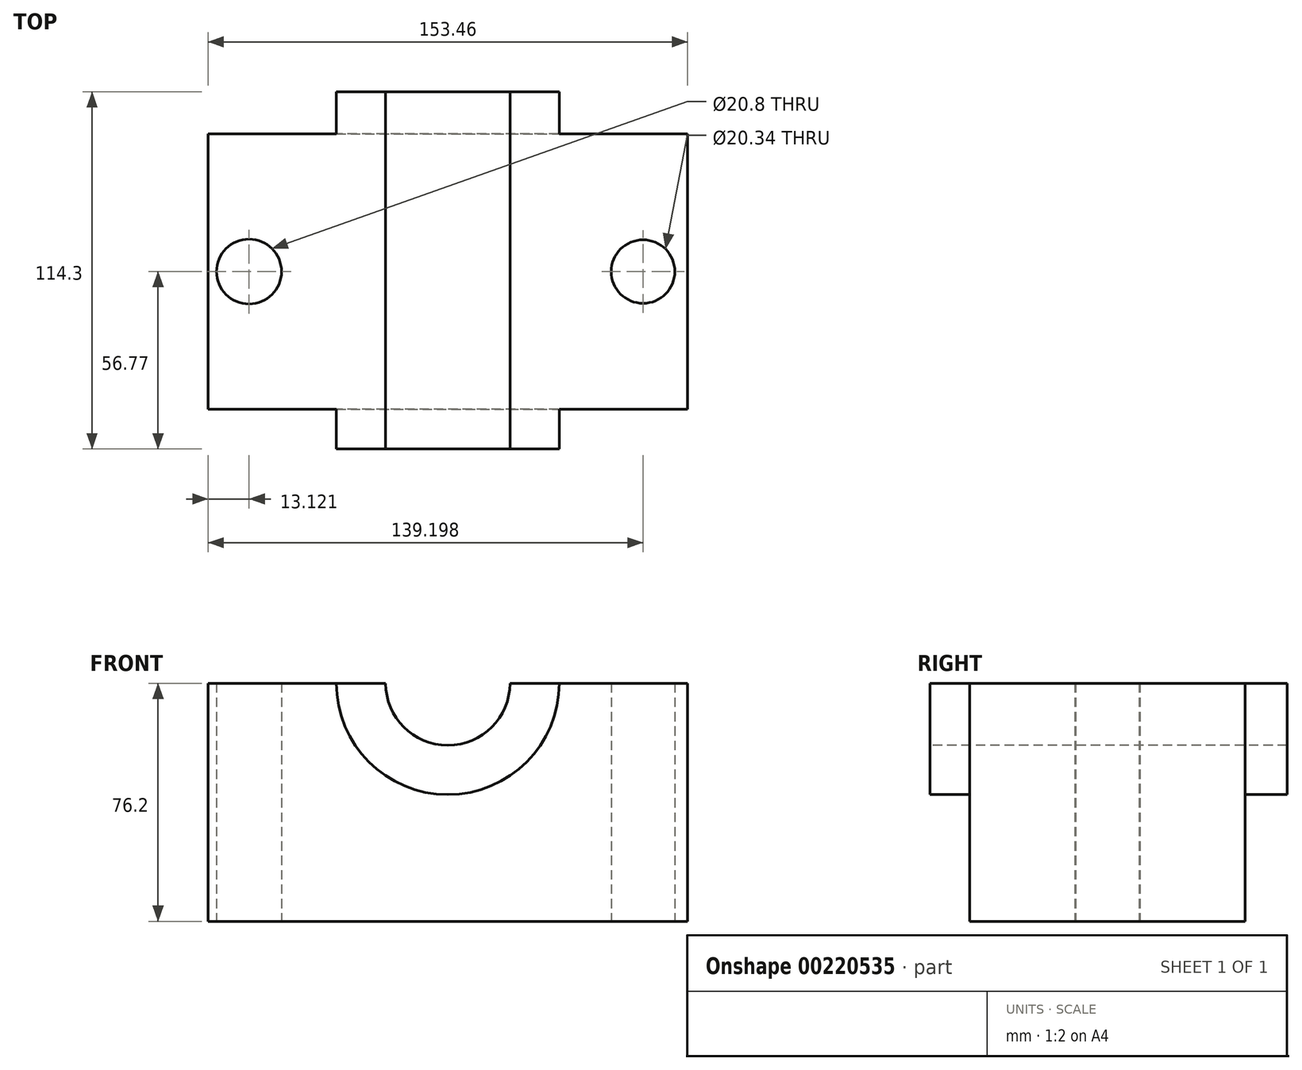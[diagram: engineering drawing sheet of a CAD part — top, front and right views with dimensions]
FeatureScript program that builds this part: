
annotation { "Feature Type Name" : "Feature", "Feature Type Description" : "" }
export const myFeature = defineFeature(function(context is Context, id is Id, definition is map)
    precondition{}
    {
        {
            var Q0;
            Q0=qCreatedBy(makeId("Top.planeOp"),FACE);
            var sketch = newSketch(context, id + "F0", { "sketchPlane" : qUnion([Q0])});
            skLineSegment(sketch, "E0.bottom", {"start": v(76.73, 44.07) * mm, "end": v(-76.73, 44.07) * mm});
            skLineSegment(sketch, "E0.top", {"start": v(76.73, -44.07) * mm, "end": v(-76.73, -44.07) * mm});
            skLineSegment(sketch, "E0.left", {"start": v(76.73, 44.07) * mm, "end": v(76.73, -44.07) * mm});
            skLineSegment(sketch, "E0.right", {"start": v(-76.73, 44.07) * mm, "end": v(-76.73, -44.07) * mm});
            skPoint(sketch, "E0.middle", {"position": v(0, 0) * mm});
            skSolve(sketch);
        }
        {
            var Q0;
            Q0=makeQuery(id+"F0.imprint","IMPRINT",FACE,{"disambiguationData":[TD([[makeQuery(id+"F0.imprint","IMPRINT",EDGE,{"derivedFrom":sQuery(id+"F0.wireOp",EDGE,"E0.bottom")}),1.0]])]});
            var sketch = newSketch(context, id + "F1", { "sketchPlane" : qUnion([Q0])});
            skCircle(sketch, "E1", {"center": v(-63.6, 0) * mm, "radius": 10.4 * mm});
            skCircle(sketch, "E2", {"center": v(62.47, 0) * mm, "radius": 10.17 * mm});
            skSolve(sketch);
        }
        {
            var Q0;
            Q0=makeQuery(id+"F0.imprint","IMPRINT",FACE,{"disambiguationData":[TD([[makeQuery(id+"F0.imprint","IMPRINT",EDGE,{"derivedFrom":sQuery(id+"F0.wireOp",EDGE,"E0.bottom")}),1.0]])]});
            extrude(context, id + "F2", {"entities" : qUnion([Q0]), "depth" : 76.2 * mm});
        }
        {
            var Q0;
            Q0=makeQuery(id+"F1.imprint","IMPRINT",FACE,{"disambiguationData":[TD([[makeQuery(id+"F1.imprint","IMPRINT",EDGE,{"derivedFrom":sQuery(id+"F1.wireOp",EDGE,"E2")}),1.0]])]});
            var Q1;
            Q1=makeQuery(id+"F1.imprint","IMPRINT",FACE,{"disambiguationData":[TD([[makeQuery(id+"F1.imprint","IMPRINT",EDGE,{"derivedFrom":sQuery(id+"F1.wireOp",EDGE,"E1")}),1.0]])]});
            extrude(context, id + "F3", {"entities" : qUnion([Q0, Q1]), "operationType" : NewBodyOperationType.REMOVE, "endBound" : BoundingType.THROUGH_ALL, "depth" : 25.4 * mm});
        }
        {
            var Q0;
            Q0=makeQuery(id+"F2.opExtrude","SWEPT_FACE",FACE,{"disambiguationData":[OSD([sQuery(id+"F0.wireOp",EDGE,"E0.top")])]});
            var sketch = newSketch(context, id + "F4", { "sketchPlane" : qUnion([Q0])});
            skCircle(sketch, "E3", {"center": v(0, 76.2) * mm, "radius": 35.65 * mm});
            skSolve(sketch);
        }
        {
            var Q0;
            {var subQ0=sQuery(id+"F4.wireOp",EDGE,"E3");var subQ1=makeQuery(id+"F2.opExtrude","CAP_EDGE",EDGE,{"disambiguationData":[OSD([sQuery(id+"F0.wireOp",EDGE,"E0.top")])],"isStart":false});var subQ2=makeQuery(id+"F4.imprint","INTERSECT",VERTEX,{"disambiguationData":[OD(0.0)],"derivedFrom":[subQ1,subQ0]});Q0=makeQuery(id+"F4.imprint","IMPRINT",FACE,{"disambiguationData":[TD([[makeQuery(id+"F4.imprint","IMPRINT",EDGE,{"disambiguationData":[TD([[subQ2,1.0]])],"derivedFrom":subQ0}),1.0]])]});}
            extrude(context, id + "F5", {"entities" : qUnion([Q0]), "operationType" : NewBodyOperationType.ADD, "oppositeDirection" : true, "depth" : 101.6 * mm});
        }
        {
            var Q0;
            Q0=makeQuery(id+"F2.opExtrude","SWEPT_FACE",FACE,{"disambiguationData":[OSD([sQuery(id+"F0.wireOp",EDGE,"E0.top")])]});
            var sketch = newSketch(context, id + "F6", { "sketchPlane" : qUnion([Q0])});
            skLineSegment(sketch, "E4", {"start": v(35.65, 76.2) * mm, "end": v(35.65, 76.2) * mm});
            skLineSegment(sketch, "E5", {"start": v(-35.65, 76.2) * mm, "end": v(-35.65, 76.2) * mm});
            skPoint(sketch, "E5.endSnap0", {"position": v(-35.65, 171.07) * mm});
            skCircle(sketch, "E6", {"center": v(0, 76.2) * mm, "radius": 35.65 * mm});
            skSolve(sketch);
        }
        {
            var Q0;
            {var subQ0=sQuery(id+"F6.wireOp",EDGE,"E6");var subQ1=makeQuery(id+"F2.opExtrude","CAP_EDGE",EDGE,{"disambiguationData":[OSD([sQuery(id+"F0.wireOp",EDGE,"E0.top")])],"isStart":false});var subQ2=makeQuery(id+"F6.imprint","INTERSECT",VERTEX,{"disambiguationData":[OD(0.0)],"derivedFrom":[subQ1,subQ0]});Q0=makeQuery(id+"F6.imprint","IMPRINT",FACE,{"disambiguationData":[TD([[makeQuery(id+"F6.imprint","IMPRINT",EDGE,{"disambiguationData":[TD([[subQ2,1.0]])],"derivedFrom":subQ0}),1.0]])]});}
            extrude(context, id + "F7", {"entities" : qUnion([Q0]), "operationType" : NewBodyOperationType.ADD, "depth" : 12.7 * mm});
        }
        {
            var Q0;
            Q0=makeQuery(id+"F7.opExtrude","CAP_FACE",FACE,{"disambiguationData":[OSD([sQuery(id+"F0.wireOp",EDGE,"E0.top"),sQuery(id+"F6.wireOp",EDGE,"E6")])],"isStart":false});
            var sketch = newSketch(context, id + "F8", { "sketchPlane" : qUnion([Q0])});
            skCircle(sketch, "E7", {"center": v(0, 76.2) * mm, "radius": 19.88 * mm});
            skSolve(sketch);
        }
        {
            var Q0;
            {var subQ0=sQuery(id+"F8.wireOp",EDGE,"E7");var subQ1=makeQuery(id+"F7.opExtrude","CAP_EDGE",EDGE,{"disambiguationData":[OSD([sQuery(id+"F0.wireOp",EDGE,"E0.top")])],"isStart":false});var subQ2=makeQuery(id+"F8.imprint","INTERSECT",VERTEX,{"disambiguationData":[OD(0.0)],"derivedFrom":[subQ1,subQ0]});Q0=makeQuery(id+"F8.imprint","IMPRINT",FACE,{"disambiguationData":[TD([[makeQuery(id+"F8.imprint","IMPRINT",EDGE,{"disambiguationData":[TD([[subQ2,1.0]])],"derivedFrom":subQ0}),1.0]])]});}
            var Q1;
            {var subQ0=sQuery(id+"F8.wireOp",EDGE,"E7");var subQ1=makeQuery(id+"F7.opExtrude","CAP_EDGE",EDGE,{"disambiguationData":[OSD([sQuery(id+"F0.wireOp",EDGE,"E0.top")])],"isStart":false});var subQ2=makeQuery(id+"F8.imprint","INTERSECT",VERTEX,{"disambiguationData":[OD(0.0)],"derivedFrom":[subQ1,subQ0]});Q1=makeQuery(id+"F8.imprint","IMPRINT",FACE,{"disambiguationData":[TD([[makeQuery(id+"F8.imprint","IMPRINT",EDGE,{"disambiguationData":[TD([[subQ2,-1.0]])],"derivedFrom":subQ0}),1.0]])]});}
            extrude(context, id + "F9", {"entities" : qUnion([Q0, Q1]), "operationType" : NewBodyOperationType.REMOVE, "endBound" : BoundingType.THROUGH_ALL, "oppositeDirection" : true, "depth" : 25.4 * mm});
        }
    });
